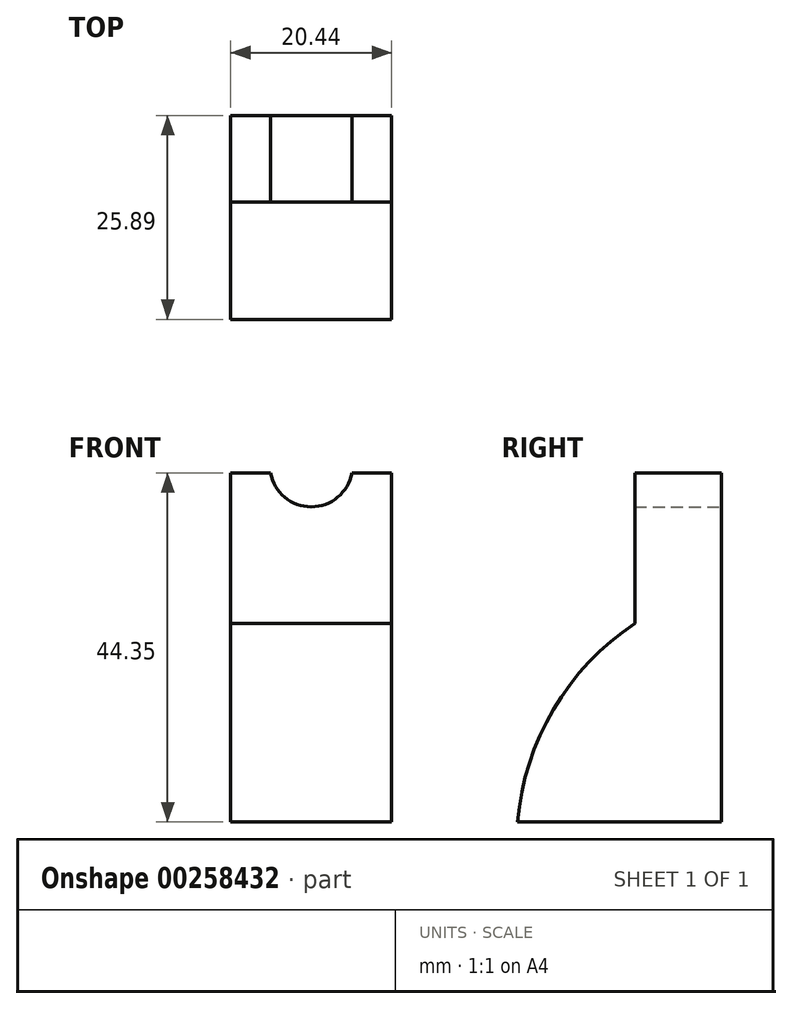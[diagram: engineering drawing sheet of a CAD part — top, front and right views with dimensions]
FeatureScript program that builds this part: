
annotation { "Feature Type Name" : "Feature", "Feature Type Description" : "" }
export const myFeature = defineFeature(function(context is Context, id is Id, definition is map)
    precondition{}
    {
        {
            var Q0;
            Q0=qCreatedBy(makeId("Front.planeOp"),FACE);
            var sketch = newSketch(context, id + "F0", { "sketchPlane" : qUnion([Q0])});
            skLineSegment(sketch, "E0.bottom", {"start": v(10.22, -37.99) * mm, "end": v(-10.22, -37.99) * mm});
            skLineSegment(sketch, "E0.left", {"start": v(10.22, -37.99) * mm, "end": v(10.22, 6.36) * mm});
            skLineSegment(sketch, "E0.right", {"start": v(-10.22, -37.99) * mm, "end": v(-10.22, 6.36) * mm});
            skPoint(sketch, "E0.middle", {"position": v(0, 0) * mm});
            skLineSegment(sketch, "E1", {"start": v(-10.22, 6.36) * mm, "end": v(-5.16, 6.36) * mm});
            skLineSegment(sketch, "E2.trimOffspring", {"start": v(5.16, 6.36) * mm, "end": v(10.22, 6.36) * mm});
            skArc(sketch, "E3.trimOffspring", {"start": v(-5.16, 6.36) * mm, "mid": v(0, 2.05) * mm, "end": v(5.16, 6.36) * mm});
            skPoint(sketch, "E4.trimOffspring.end.orphan", {"position": v(-10.22, 37.99) * mm});
            skPoint(sketch, "E5.trimOffspring.end.orphan", {"position": v(10.22, 37.99) * mm});
            skSolve(sketch);
        }
        {
            var Q0;
            Q0 = qSketchRegion(id + "F0", true);
            extrude(context, id + "F1", {"entities" : qUnion([Q0]), "depth" : 11 * mm});
        }
        {
            var Q0;
            Q0=makeQuery(id+"F1.opExtrude","CAP_FACE",FACE,{"disambiguationData":[OSD([sQuery(id+"F0.wireOp",EDGE,"E0.bottom"),sQuery(id+"F0.wireOp",EDGE,"E0.left"),sQuery(id+"F0.wireOp",EDGE,"E0.right"),sQuery(id+"F0.wireOp",EDGE,"E1"),sQuery(id+"F0.wireOp",EDGE,"E2.trimOffspring"),sQuery(id+"F0.wireOp",EDGE,"E3.trimOffspring")])],"isStart":false});
            var sketch = newSketch(context, id + "F2", { "sketchPlane" : qUnion([Q0])});
            skLineSegment(sketch, "E6.bottom", {"start": v(-10.22, -37.99) * mm, "end": v(10.22, -37.99) * mm});
            skLineSegment(sketch, "E6.top", {"start": v(-10.22, -12.78) * mm, "end": v(10.22, -12.78) * mm});
            skLineSegment(sketch, "E6.left", {"start": v(-10.22, -37.99) * mm, "end": v(-10.22, -12.78) * mm});
            skLineSegment(sketch, "E6.right", {"start": v(10.22, -37.99) * mm, "end": v(10.22, -12.78) * mm});
            skSolve(sketch);
        }
        {
            var Q0;
            Q0 = qSketchRegion(id + "F2", true);
            extrude(context, id + "F3", {"entities" : qUnion([Q0]), "operationType" : NewBodyOperationType.ADD, "depth" : 15 * mm});
        }
        {
            var Q0;
            Q0=makeQuery(id+"F3.opExtrude","CAP_EDGE",EDGE,{"disambiguationData":[OSD([sQuery(id+"F2.wireOp",EDGE,"E6.top")])],"isStart":false});
            fillet(context, id + "F4", {"entities" : qUnion([Q0]), "radius" : 33.56 * mm, "tangentPropagation" : true, "allowEdgeOverflow" : false});
        }
    });
